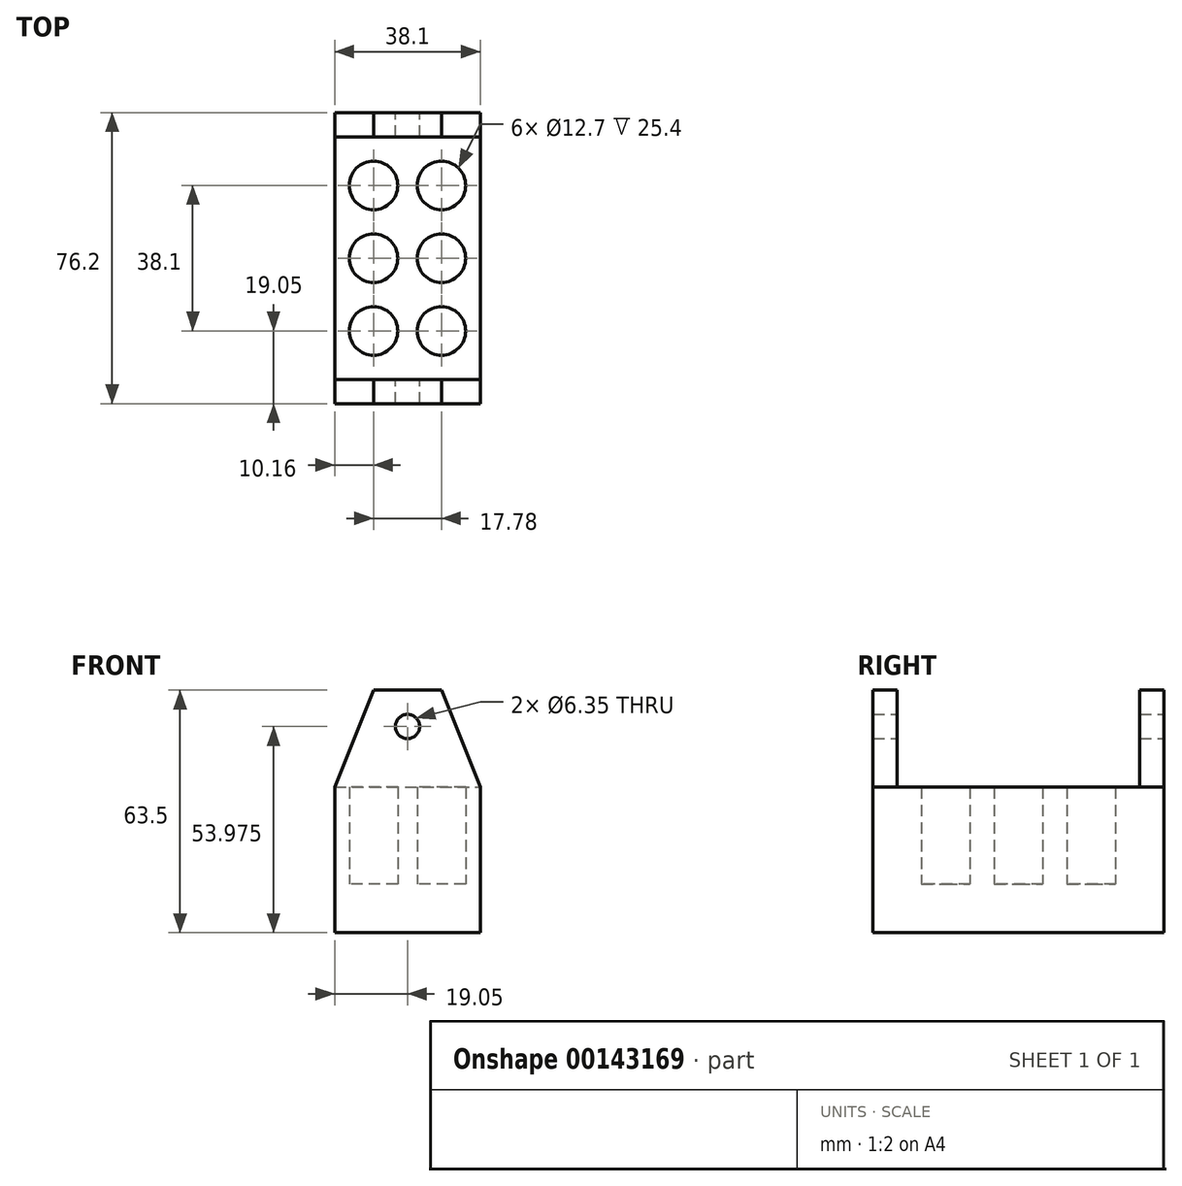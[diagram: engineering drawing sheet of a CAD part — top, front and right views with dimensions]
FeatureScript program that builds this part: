
annotation { "Feature Type Name" : "Feature", "Feature Type Description" : "" }
export const myFeature = defineFeature(function(context is Context, id is Id, definition is map)
    precondition{}
    {
        {
            var Q0;
            Q0=qCreatedBy(makeId("Top.planeOp"),FACE);
            var sketch = newSketch(context, id + "F0", { "sketchPlane" : qUnion([Q0])});
            skLineSegment(sketch, "E0.bottom", {"start": v(0, 0) * mm, "end": v(38.1, 0) * mm});
            skLineSegment(sketch, "E0.top", {"start": v(0, 76.2) * mm, "end": v(38.1, 76.2) * mm});
            skLineSegment(sketch, "E0.left", {"start": v(0, 0) * mm, "end": v(0, 76.2) * mm});
            skLineSegment(sketch, "E0.right", {"start": v(38.1, 0) * mm, "end": v(38.1, 76.2) * mm});
            skCircle(sketch, "E1", {"center": v(10.16, 38.1) * mm, "radius": 6.35 * mm});
            skCircle(sketch, "E2", {"center": v(10.16, 57.15) * mm, "radius": 6.35 * mm});
            skCircle(sketch, "E3", {"center": v(10.16, 19.05) * mm, "radius": 6.35 * mm});
            skCircle(sketch, "E4", {"center": v(27.94, 19.05) * mm, "radius": 6.35 * mm});
            skCircle(sketch, "E5", {"center": v(27.94, 38.1) * mm, "radius": 6.35 * mm});
            skCircle(sketch, "E6", {"center": v(27.94, 57.15) * mm, "radius": 6.35 * mm});
            skSolve(sketch);
        }
        {
            var Q0;
            Q0=makeQuery(id+"F0.imprint","IMPRINT",FACE,{"disambiguationData":[TD([[makeQuery(id+"F0.imprint","IMPRINT",EDGE,{"derivedFrom":sQuery(id+"F0.wireOp",EDGE,"E0.bottom")}),1.0]])]});
            extrude(context, id + "F1", {"entities" : qUnion([Q0]), "depth" : 38.1 * mm});
        }
        {
            var Q0;
            Q0=makeQuery(id+"F0.imprint","IMPRINT",FACE,{"disambiguationData":[TD([[makeQuery(id+"F0.imprint","IMPRINT",EDGE,{"derivedFrom":sQuery(id+"F0.wireOp",EDGE,"E2")}),1.0]])]});
            var Q1;
            Q1=makeQuery(id+"F0.imprint","IMPRINT",FACE,{"disambiguationData":[TD([[makeQuery(id+"F0.imprint","IMPRINT",EDGE,{"derivedFrom":sQuery(id+"F0.wireOp",EDGE,"E6")}),1.0]])]});
            var Q2;
            Q2=makeQuery(id+"F0.imprint","IMPRINT",FACE,{"disambiguationData":[TD([[makeQuery(id+"F0.imprint","IMPRINT",EDGE,{"derivedFrom":sQuery(id+"F0.wireOp",EDGE,"E5")}),1.0]])]});
            var Q3;
            Q3=makeQuery(id+"F0.imprint","IMPRINT",FACE,{"disambiguationData":[TD([[makeQuery(id+"F0.imprint","IMPRINT",EDGE,{"derivedFrom":sQuery(id+"F0.wireOp",EDGE,"E3")}),1.0]])]});
            var Q4;
            Q4=makeQuery(id+"F0.imprint","IMPRINT",FACE,{"disambiguationData":[TD([[makeQuery(id+"F0.imprint","IMPRINT",EDGE,{"derivedFrom":sQuery(id+"F0.wireOp",EDGE,"E4")}),1.0]])]});
            var Q5;
            Q5=makeQuery(id+"F0.imprint","IMPRINT",FACE,{"disambiguationData":[TD([[makeQuery(id+"F0.imprint","IMPRINT",EDGE,{"derivedFrom":sQuery(id+"F0.wireOp",EDGE,"E1")}),1.0]])]});
            extrude(context, id + "F2", {"entities" : qUnion([Q0, Q1, Q2, Q3, Q4, Q5]), "operationType" : NewBodyOperationType.ADD, "depth" : 12.7 * mm});
        }
        {
            var Q0;
            Q0=makeQuery(id+"F1.opExtrude","CAP_FACE",FACE,{"disambiguationData":[OSD([sQuery(id+"F0.wireOp",EDGE,"E0.bottom"),sQuery(id+"F0.wireOp",EDGE,"E0.top"),sQuery(id+"F0.wireOp",EDGE,"E0.left"),sQuery(id+"F0.wireOp",EDGE,"E0.right"),sQuery(id+"F0.wireOp",EDGE,"E1"),sQuery(id+"F0.wireOp",EDGE,"E2"),sQuery(id+"F0.wireOp",EDGE,"E3"),sQuery(id+"F0.wireOp",EDGE,"E4"),sQuery(id+"F0.wireOp",EDGE,"E5"),sQuery(id+"F0.wireOp",EDGE,"E6")])],"isStart":false});
            var sketch = newSketch(context, id + "F3", { "sketchPlane" : qUnion([Q0])});
            skLineSegment(sketch, "E7.bottom", {"start": v(0, 0) * mm, "end": v(38.1, 0) * mm});
            skLineSegment(sketch, "E7.top", {"start": v(0, 6.35) * mm, "end": v(38.1, 6.35) * mm});
            skLineSegment(sketch, "E7.left", {"start": v(0, 0) * mm, "end": v(0, 6.35) * mm});
            skLineSegment(sketch, "E7.right", {"start": v(38.1, 0) * mm, "end": v(38.1, 6.35) * mm});
            skLineSegment(sketch, "E8.bottom", {"start": v(0, 76.2) * mm, "end": v(38.1, 76.2) * mm});
            skLineSegment(sketch, "E8.top", {"start": v(0, 69.85) * mm, "end": v(38.1, 69.85) * mm});
            skLineSegment(sketch, "E8.left", {"start": v(0, 76.2) * mm, "end": v(0, 69.85) * mm});
            skLineSegment(sketch, "E8.right", {"start": v(38.1, 76.2) * mm, "end": v(38.1, 69.85) * mm});
            skSolve(sketch);
        }
        {
            var Q0;
            Q0=makeQuery(id+"F3.imprint","IMPRINT",FACE,{"disambiguationData":[TD([[makeQuery(id+"F3.imprint","IMPRINT",EDGE,{"derivedFrom":sQuery(id+"F3.wireOp",EDGE,"E8.bottom")}),-1.0]])]});
            var Q1;
            Q1=makeQuery(id+"F3.imprint","IMPRINT",FACE,{"disambiguationData":[TD([[makeQuery(id+"F3.imprint","IMPRINT",EDGE,{"derivedFrom":sQuery(id+"F3.wireOp",EDGE,"E7.bottom")}),1.0]])]});
            extrude(context, id + "F4", {"entities" : qUnion([Q0, Q1]), "operationType" : NewBodyOperationType.ADD, "depth" : 25.4 * mm});
        }
        {
            var Q0;
            Q0=makeQuery(id+"F4.opExtrude","CAP_EDGE",EDGE,{"disambiguationData":[OSD([sQuery(id+"F3.wireOp",EDGE,"E8.right")])],"isStart":false});
            var Q1;
            Q1=makeQuery(id+"F4.opExtrude","CAP_EDGE",EDGE,{"disambiguationData":[OSD([sQuery(id+"F3.wireOp",EDGE,"E8.left")])],"isStart":false});
            chamfer(context, id + "F5", {"entities" : qUnion([Q0, Q1]), "chamferType" : ChamferType.TWO_OFFSETS, "width1" : 25.4 * mm, "oppositeDirection" : true, "width2" : 10.16 * mm, "tangentPropagation" : true});
        }
        {
            var Q0;
            Q0=makeQuery(id+"F4.opExtrude","CAP_EDGE",EDGE,{"disambiguationData":[OSD([sQuery(id+"F3.wireOp",EDGE,"E7.right")])],"isStart":false});
            var Q1;
            Q1=makeQuery(id+"F4.opExtrude","CAP_EDGE",EDGE,{"disambiguationData":[OSD([sQuery(id+"F3.wireOp",EDGE,"E7.left")])],"isStart":false});
            chamfer(context, id + "F6", {"entities" : qUnion([Q0, Q1]), "chamferType" : ChamferType.TWO_OFFSETS, "width1" : 25.4 * mm, "oppositeDirection" : true, "width2" : 10.16 * mm, "tangentPropagation" : true});
        }
        {
            var Q0;
            Q0=makeQuery(id+"F4.boolean.opBoolean","MERGE",FACE,{"derivedFrom":[makeQuery(id+"F1.opExtrude","SWEPT_FACE",FACE,{"disambiguationData":[OSD([sQuery(id+"F0.wireOp",EDGE,"E0.top")])]}),makeQuery(id+"F4.opExtrude","SWEPT_FACE",FACE,{"disambiguationData":[OSD([sQuery(id+"F3.wireOp",EDGE,"E8.bottom")])]})]});
            var sketch = newSketch(context, id + "F7", { "sketchPlane" : qUnion([Q0])});
            skCircle(sketch, "E9", {"center": v(-19.05, 53.98) * mm, "radius": 3.18 * mm});
            skSolve(sketch);
        }
        {
            var Q0;
            Q0=makeQuery(id+"F7.imprint","IMPRINT",FACE,{"disambiguationData":[TD([[makeQuery(id+"F7.imprint","IMPRINT",EDGE,{"derivedFrom":sQuery(id+"F7.wireOp",EDGE,"E9")}),1.0]])]});
            extrude(context, id + "F8", {"entities" : qUnion([Q0]), "operationType" : NewBodyOperationType.REMOVE, "oppositeDirection" : true, "depth" : 105.84 * mm});
        }
    });
